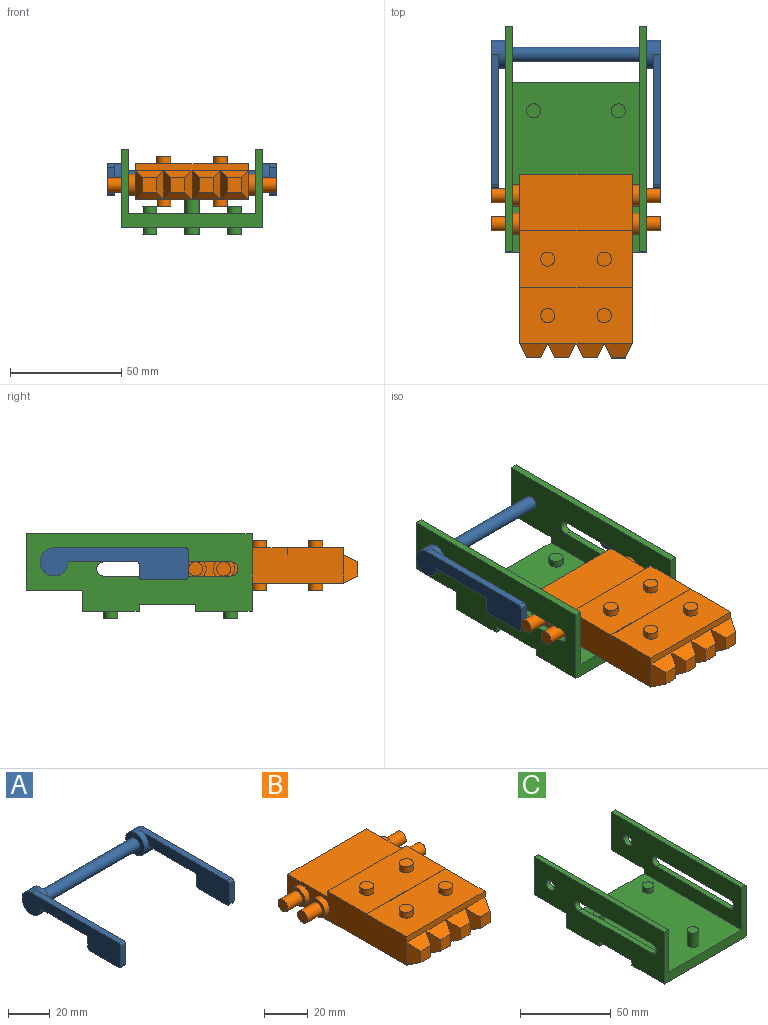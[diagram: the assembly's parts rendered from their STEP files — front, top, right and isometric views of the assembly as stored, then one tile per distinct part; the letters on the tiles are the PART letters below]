
ASSEMBLY  parts=3 mates=2
PART A: 27 faces, bbox 76.2x66.7x14.3 mm
  f0: cylinder r=6.35mm len=12.7mm, axis (-1,0,0), area 221.7mm2, adj f1,f2,f7,f8,f12
  f1: plane 66.68x14.29mm, normal (1,0,0), area 653mm2, adj f0,f3,f4,f5,f6,f7,f8,f9
  f2: plane 12.7x12.7mm, normal (-1,0,0), area 95mm2, adj f0,f13
  f3: plane 19.05x3.18mm, normal (0,0,-1), area 60.5mm2, adj f1,f4,f11,f12
  f4: cylinder r=1.59mm len=3.18mm, axis (-1,0,0), area 7.9mm2, adj f1,f3,f5,f12
  f5: plane 5.56x3.18mm, normal (0,1,0), area 17.6mm2, adj f1,f4,f6,f12
  f6: cylinder r=0.79mm len=3.18mm, axis (-1,0,0), area 4mm2, adj f1,f5,f7,f12
  f7: plane 30.96x3.18mm, normal (0,0,-1), area 98.3mm2, adj f0,f1,f6,f12
  f8: plane 58.74x3.18mm, normal (0,0,1), area 186.5mm2, adj f0,f1,f9,f12
  f9: cylinder r=1.59mm len=3.18mm, axis (-1,0,0), area 7.9mm2, adj f1,f8,f10,f12
  f10: plane 11.11x3.18mm, normal (0,-1,0), area 35.3mm2, adj f1,f9,f11,f12
  f11: cylinder r=1.59mm len=3.18mm, axis (-1,0,0), area 7.9mm2, adj f1,f3,f10,f12
  f12: plane 60.33x14.29mm, normal (-1,0,0), area 526.3mm2, adj f0,f3,f4,f5,f6,f7,f8,f9
  f13: cylinder r=3.17mm len=63.5mm, axis (-1,0,0), area 1266.8mm2, adj f2,f16
  f14: cylinder r=6.35mm len=12.7mm, axis (1,0,0), area 221.7mm2, adj f15,f16,f21,f22,f26
  f15: plane 66.68x14.29mm, normal (-1,0,0), area 653mm2, adj f14,f17,f18,f19,f20,f21,f22,f23
  f16: plane 12.7x12.7mm, normal (1,0,0), area 95mm2, adj f13,f14
  f17: plane 19.05x3.18mm, normal (0,0,-1), area 60.5mm2, adj f15,f18,f25,f26
  f18: cylinder r=1.59mm len=3.18mm, axis (1,0,0), area 7.9mm2, adj f15,f17,f19,f26
  f19: plane 5.56x3.18mm, normal (0,1,0), area 17.6mm2, adj f15,f18,f20,f26
  f20: cylinder r=0.79mm len=3.18mm, axis (1,0,0), area 4mm2, adj f15,f19,f21,f26
  f21: plane 30.96x3.18mm, normal (0,0,-1), area 98.3mm2, adj f14,f15,f20,f26
  f22: plane 58.74x3.18mm, normal (0,0,1), area 186.5mm2, adj f14,f15,f23,f26
  f23: cylinder r=1.59mm len=3.18mm, axis (1,0,0), area 7.9mm2, adj f15,f22,f24,f26
  f24: plane 11.11x3.18mm, normal (0,-1,0), area 35.3mm2, adj f15,f23,f25,f26
  f25: cylinder r=1.59mm len=3.18mm, axis (1,0,0), area 7.9mm2, adj f15,f17,f24,f26
  f26: plane 60.33x14.29mm, normal (1,0,0), area 526.3mm2, adj f14,f17,f18,f19,f20,f21,f22,f23
PART B: 69 faces, bbox 76.2x82.6x22.2 mm
  f0: plane 6.35x6.35mm, normal (0,-1,0), area 40.3mm2, adj f6,f7,f67,f68
  f1: plane 6.35x6.35mm, normal (0,-1,0), area 40.3mm2, adj f8,f9,f65,f66
  f2: plane 6.35x6.35mm, normal (0,-1,0), area 40.3mm2, adj f10,f11,f63,f64
  f3: plane 6.35x6.35mm, normal (0,-1,0), area 40.3mm2, adj f5,f12,f61,f62
  f4: plane 76.2x50.8mm, normal (0,0,-1), area 3349.7mm2, adj f14,f15,f16,f34,f35,f36,f37,f47
  f5: plane 12.7x6.35mm, normal (0.89,-0.45,0), area 67.6mm2, adj f3,f6,f61,f62
  f6: plane 12.7x6.35mm, normal (-0.89,-0.45,0), area 67.6mm2, adj f0,f5,f67,f68
  f7: plane 12.7x6.35mm, normal (0.89,-0.45,0), area 67.6mm2, adj f0,f8,f67,f68
  f8: plane 12.7x6.35mm, normal (-0.89,-0.45,0), area 67.6mm2, adj f1,f7,f65,f66
  f9: plane 12.7x6.35mm, normal (0.89,-0.45,0), area 67.6mm2, adj f1,f14,f65,f66
  f10: plane 12.7x6.35mm, normal (-0.89,-0.45,0), area 67.6mm2, adj f2,f16,f63,f64
  f11: plane 12.7x6.35mm, normal (0.89,-0.45,0), area 67.6mm2, adj f2,f12,f63,f64
  f12: plane 12.7x6.35mm, normal (-0.89,-0.45,0), area 67.6mm2, adj f3,f11,f61,f62
  f13: plane 50.8x0.13mm, normal (0,0,1), area 6.5mm2, adj f14,f16,f40,f43
  f14: plane 76.2x15.88mm, normal (1,0,0), area 986.1mm2, adj f4,f9,f13,f15,f17,f19,f27,f39
  f15: plane 50.8x12.7mm, normal (0,1,0), area 645.2mm2, adj f4,f14,f16,f17
  f16: plane 76.2x15.88mm, normal (-1,0,0), area 986.1mm2, adj f4,f10,f13,f15,f17,f20,f28,f39
  f17: plane 50.8x25.4mm, normal (0,0,1), area 1290.3mm2, adj f14,f15,f16,f39
  f18: plane 9.53x9.53mm, normal (1,0,0), area 39.6mm2, adj f19,f25
  f19: cylinder r=4.76mm len=9.53mm, axis (-1,0,0), area 95mm2, adj f14,f18
  f20: cylinder r=4.76mm len=9.53mm, axis (-1,0,0), area 95mm2, adj f16,f21
  f21: plane 9.53x9.53mm, normal (-1,0,0), area 39.6mm2, adj f20,f23
  f22: plane 6.35x6.35mm, normal (-1,0,0), area 31.7mm2, adj f23
  f23: cylinder r=3.17mm len=9.53mm, axis (-1,0,0), area 190mm2, adj f21,f22
  f24: plane 6.35x6.35mm, normal (1,0,0), area 31.7mm2, adj f25
  f25: cylinder r=3.17mm len=9.53mm, axis (-1,0,0), area 190mm2, adj f18,f24
  f26: plane 9.53x9.53mm, normal (1,0,0), area 39.6mm2, adj f27,f33
  f27: cylinder r=4.76mm len=9.53mm, axis (-1,0,0), area 95mm2, adj f14,f26
  f28: cylinder r=4.76mm len=9.53mm, axis (-1,0,0), area 95mm2, adj f16,f29
  f29: plane 9.53x9.53mm, normal (-1,0,0), area 39.6mm2, adj f28,f31
  f30: plane 6.35x6.35mm, normal (-1,0,0), area 31.7mm2, adj f31
  f31: cylinder r=3.17mm len=9.53mm, axis (-1,0,0), area 190mm2, adj f29,f30
  f32: plane 6.35x6.35mm, normal (1,0,0), area 31.7mm2, adj f33
  f33: cylinder r=3.17mm len=9.53mm, axis (-1,0,0), area 190mm2, adj f26,f32
  f34: cylinder r=3.17mm len=6.35mm, axis (0,0,-1), area 31.7mm2, adj f4,f35,f37,f38
  f35: plane 57.15x3.18mm, normal (1,0,0), area 181.5mm2, adj f4,f34,f36,f38
  f36: cylinder r=3.17mm len=6.35mm, axis (0,0,-1), area 31.7mm2, adj f4,f35,f37,f38
  f37: plane 57.15x3.18mm, normal (-1,0,0), area 181.5mm2, adj f4,f34,f36,f38
  f38: plane 63.5x6.35mm, normal (0,0,-1), area 394.6mm2, adj f34,f35,f36,f37
  f39: plane 50.8x3.18mm, normal (0,1,0), area 161.3mm2, adj f14,f16,f17,f41
  f40: plane 50.8x3.18mm, normal (0,-1,0), area 161.3mm2, adj f13,f14,f16,f41
  f41: plane 50.8x25.27mm, normal (0,0,1), area 1220.5mm2, adj f14,f16,f39,f40,f46,f58
  f42: plane 50.8x3.18mm, normal (0,-1,0), area 161.3mm2, adj f14,f16,f44,f62,f64,f66,f68
  f43: plane 50.8x3.18mm, normal (0,1,0), area 161.3mm2, adj f13,f14,f16,f44
  f44: plane 50.8x25.4mm, normal (0,0,1), area 1227mm2, adj f14,f16,f42,f43,f50,f54
  f45: plane 6.35x6.35mm, normal (0,0,1), area 31.7mm2, adj f46
  f46: cylinder r=3.17mm len=6.35mm, axis (0,0,-1), area 63.3mm2, adj f41,f45
  f47: cylinder r=3.17mm len=6.35mm, axis (0,0,-1), area 63.3mm2, adj f4,f48
  f48: plane 6.35x6.35mm, normal (0,0,-1), area 31.7mm2, adj f47
  f49: plane 6.35x6.35mm, normal (0,0,1), area 31.7mm2, adj f50
  f50: cylinder r=3.17mm len=6.35mm, axis (0,0,-1), area 63.3mm2, adj f44,f49
  f51: cylinder r=3.17mm len=6.35mm, axis (0,0,-1), area 63.3mm2, adj f4,f52
  f52: plane 6.35x6.35mm, normal (0,0,-1), area 31.7mm2, adj f51
  f53: plane 6.35x6.35mm, normal (0,0,1), area 31.7mm2, adj f54
  f54: cylinder r=3.17mm len=6.35mm, axis (0,0,-1), area 63.3mm2, adj f44,f53
  f55: cylinder r=3.17mm len=6.35mm, axis (0,0,-1), area 63.3mm2, adj f4,f56
  f56: plane 6.35x6.35mm, normal (0,0,-1), area 31.7mm2, adj f55
  f57: plane 6.35x6.35mm, normal (0,0,1), area 31.7mm2, adj f58
  f58: cylinder r=3.17mm len=6.35mm, axis (0,0,-1), area 63.3mm2, adj f41,f57
  f59: cylinder r=3.17mm len=6.35mm, axis (0,0,-1), area 63.3mm2, adj f4,f60
  f60: plane 6.35x6.35mm, normal (0,0,-1), area 31.7mm2, adj f59
  f61: plane 12.7x6.35mm, normal (0,-0.45,-0.89), area 67.6mm2, adj f3,f4,f5,f12
  f62: plane 12.7x6.35mm, normal (0,-0.45,0.89), area 67.6mm2, adj f3,f5,f12,f42
  f63: plane 12.7x6.35mm, normal (0,-0.45,-0.89), area 67.6mm2, adj f2,f4,f10,f11
  f64: plane 12.7x6.35mm, normal (0,-0.45,0.89), area 67.6mm2, adj f2,f10,f11,f42
  f65: plane 12.7x6.35mm, normal (0,-0.45,-0.89), area 67.6mm2, adj f1,f4,f8,f9
  f66: plane 12.7x6.35mm, normal (0,-0.45,0.89), area 67.6mm2, adj f1,f8,f9,f42
  f67: plane 12.7x6.35mm, normal (0,-0.45,-0.89), area 67.6mm2, adj f0,f4,f6,f7
  f68: plane 12.7x6.35mm, normal (0,-0.45,0.89), area 67.6mm2, adj f0,f6,f7,f42
PART C: 40 faces, bbox 63.5x101.6x38.1 mm
  f0: plane 63.5x25.4mm, normal (0,0,-1), area 1612.9mm2, adj f2,f8,f26,f30
  f1: plane 63.5x9.53mm, normal (0,1,0), area 423.4mm2, adj f2,f4,f5,f6,f8,f20,f22,f31
  f2: plane 101.6x34.93mm, normal (1,0,0), area 2799.6mm2, adj f0,f1,f3,f9,f14,f15,f16,f17
  f3: plane 101.6x3.18mm, normal (0,0,1), area 322.6mm2, adj f2,f4,f9,f21
  f4: plane 101.6x28.58mm, normal (-1,0,0), area 2396.3mm2, adj f1,f3,f5,f9,f14,f15,f16,f17
  f5: plane 76.2x57.15mm, normal (0,0,1), area 4259.8mm2, adj f1,f4,f6,f9,f18,f34,f38
  f6: plane 101.6x28.58mm, normal (1,0,0), area 2396.3mm2, adj f1,f5,f7,f9,f10,f11,f12,f13
  f7: plane 101.6x3.18mm, normal (0,0,1), area 322.6mm2, adj f6,f8,f9,f23
  f8: plane 101.6x34.93mm, normal (-1,0,0), area 2799.6mm2, adj f0,f1,f7,f9,f10,f11,f12,f13
  f9: plane 63.5x34.93mm, normal (0,-1,0), area 584.7mm2, adj f2,f3,f4,f5,f6,f7,f8,f27
  f10: plane 57.15x3.18mm, normal (0,0,1), area 181.5mm2, adj f6,f8,f11,f13
  f11: cylinder r=3.17mm len=6.35mm, axis (1,0,0), area 31.7mm2, adj f6,f8,f10,f12
  f12: plane 57.15x3.18mm, normal (0,0,-1), area 181.5mm2, adj f6,f8,f11,f13
  f13: cylinder r=3.17mm len=6.35mm, axis (1,0,0), area 31.7mm2, adj f6,f8,f10,f12
  f14: cylinder r=3.17mm len=6.35mm, axis (1,0,0), area 31.7mm2, adj f2,f4,f15,f17
  f15: plane 57.15x3.18mm, normal (0,0,-1), area 181.5mm2, adj f2,f4,f14,f16
  f16: cylinder r=3.17mm len=6.35mm, axis (1,0,0), area 31.7mm2, adj f2,f4,f15,f17
  f17: plane 57.15x3.18mm, normal (0,0,1), area 181.5mm2, adj f2,f4,f14,f16
  f18: cylinder r=3.17mm len=9.53mm, axis (0,0,-1), area 190mm2, adj f5,f19
  f19: plane 6.35x6.35mm, normal (0,0,1), area 31.7mm2, adj f18
  f20: plane 25.4x3.18mm, normal (0,0,-1), area 80.6mm2, adj f1,f2,f4,f21
  f21: plane 25.4x3.18mm, normal (0,1,0), area 80.6mm2, adj f2,f3,f4,f20
  f22: plane 25.4x3.18mm, normal (0,0,-1), area 80.6mm2, adj f1,f6,f8,f23
  f23: plane 25.4x3.18mm, normal (0,1,0), area 80.6mm2, adj f6,f7,f8,f22
  f24: cylinder r=3.17mm len=6.35mm, axis (1,0,0), area 63.3mm2, adj f6,f8
  f25: cylinder r=3.17mm len=6.35mm, axis (1,0,0), area 63.3mm2, adj f2,f4
  f26: plane 63.5x3.18mm, normal (0,1,0), area 201.6mm2, adj f0,f2,f8,f27
  f27: plane 63.5x25.4mm, normal (0,0,-1), area 1581.2mm2, adj f2,f8,f9,f26,f29
  f28: plane 6.35x6.35mm, normal (0,0,-1), area 31.7mm2, adj f29
  f29: cylinder r=3.17mm len=6.35mm, axis (0,0,-1), area 63.3mm2, adj f27,f28
  f30: plane 63.5x3.18mm, normal (0,-1,0), area 201.6mm2, adj f0,f2,f8,f31
  f31: plane 63.5x25.4mm, normal (0,0,-1), area 1549.6mm2, adj f1,f2,f8,f30,f33,f37
  f32: plane 6.35x6.35mm, normal (0,0,-1), area 31.7mm2, adj f33
  f33: cylinder r=3.17mm len=6.35mm, axis (0,0,-1), area 63.3mm2, adj f31,f32
  f34: cylinder r=3.17mm len=6.35mm, axis (0,0,-1), area 63.3mm2, adj f5,f35
  f35: plane 6.35x6.35mm, normal (0,0,1), area 31.7mm2, adj f34
  f36: plane 6.35x6.35mm, normal (0,0,-1), area 31.7mm2, adj f37
  f37: cylinder r=3.17mm len=6.35mm, axis (0,0,-1), area 63.3mm2, adj f31,f36
  f38: cylinder r=3.17mm len=6.35mm, axis (0,0,-1), area 63.3mm2, adj f5,f39
  f39: plane 6.35x6.35mm, normal (0,0,1), area 31.7mm2, adj f38
PLACE A rot(axis=(1,0,0),0deg) t=(-4.16,-80.17,0.84)mm
PLACE B t=(-4.16,-121.45,0.84)mm
PLACE C t=(-4.16,-80.17,0.84)mm fixed
MATE revolute C.f24 <-> A.f0  axis (-1,0,0) through (-35.91,-29.37,19.89)mm
MATE pin_slot C.f13 <-> B.f19  axis (-1,0,0) through (24.41,-51.6,16.72)mm
